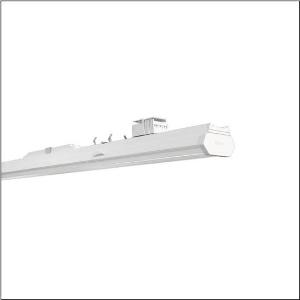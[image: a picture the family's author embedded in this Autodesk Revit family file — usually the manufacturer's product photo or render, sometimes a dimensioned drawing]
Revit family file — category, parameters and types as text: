
# Revit family: licross_r__11_protected_ho_51td12dn4fxm3s_901f
name_source: partatom
category: Lighting Fixtures
units: mm (PartAtom-declared; Revit-internal decimal feet)

## family parameters
Cut with Voids When Loaded = No
Host = Face
Light Source = No
Part Type = Normal
Room Calculation Point = No
Round Connector Dimension = Use Diameter
Shared = No

## types (1)
- --- (1 x LED, 970 lm, 7.4 W, 4000K)
    Apparent Load = 7 VA
    CIE Flux Codes = 70 91 97 98 100
    Color Rendering = 80
    Color Temperature = 4000K
    Default Elevation = 1800 mm
    Description = Licross® 11 Protected HO, luminaire insert, of sheet steel, galvanised, coil coated, white, length: 1.500mm, width: 90mm, height: 101mm, LED rated luminous flux: 15.270lm, light colour: 840, control gear: DALI 2 (for two DALI lines), with plug, 6-pole, with phase selection, for trunking rail, 14-core, mains connection: 220..240V, AC, 50/60Hz, rated input power: 91W, for trunking rail, 14-core, halogen-free wiring, for emergency light function, converter,control gear: single battery element, battery: LiFePO4, 9Ah, primary light control with lens, of plastic, primary optical cover: cover, of PMMA, light emission: direct distribution, primary light characteristic: symmetric, protection rating (complete): IP54, insulation class (complete): insulation class I (protective earthing), certification: CE, UKCA, protection symbol: D if used in an environment with non-conductive dust loads with corresponding accessories, impact resistance: IK06, permissible ambient temperature for indoor applications: +5..+30°C, standard: EN 60598-2-22, LABS conformity tested according to VDMA 24364:2018-05, reducing of maximum allowable ambient temperature of 5°C with ceiling mounting, corresponds to IFS (International Featured Standards) requirements for safety and quality in the food industry, packaging unit: 1 piece
    Height = 92 mm
    Lamp = 1 x LED
    Lamp Light Flux = 970 lm
    Lamp Power = 7.4 W
    Lamp count = 1
    Length = 1500 mm
    Luminous efficacy = 131 lm/W
    Manufacturer = Siteco
    ModVariant = No
    Model = 51TD12DN4FXM3S
    Mounting Place = Ceiling
    Mounting Type = Pendant
    Number of Poles = 1
    OnlyDefault = Yes
    Power Factor = 1
    Product Name = Licross® 11 Protected HO
    Product group = luminaire insert
    ProductGroupID = 901
    Protection Class = Protection class I
    Protection Degree = IP 54
    RLX_Detail_Level = 1
    RLX_Emergency_Light_Flux = 0 lm
    RLX_Emergency_Type = 0
    RLX_Emergency_Type_DB = No
    RlxData = <blob elided: 24949 chars, md5=0ac6771f>
    Socket = socket
    Standby Power = 0 W
    System Light Flux = 970 lm
    System Power = 7 W
    Type Comments = : emergency light operation: 3 h
    Type Image = l_1256145.jpg
    URL = http://relux.com
    VarID = @adj_059797
    Voltage = 0 V
    Weight = 0.00 kg
    Width = 88 mm

## geometry (parser evidence)
native form markers: Blend x4, Sweep x11
no freeform markers — native parametric forms only
